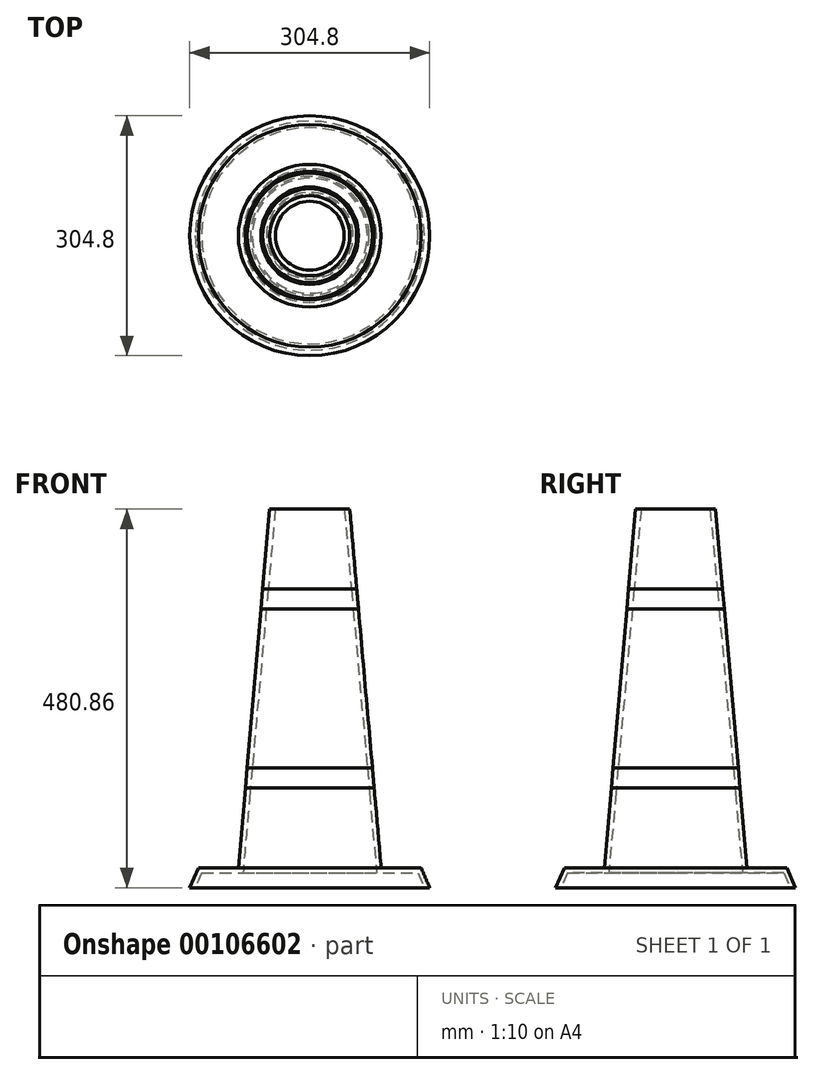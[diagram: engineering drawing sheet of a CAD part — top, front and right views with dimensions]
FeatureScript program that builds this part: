
annotation { "Feature Type Name" : "Feature", "Feature Type Description" : "" }
export const myFeature = defineFeature(function(context is Context, id is Id, definition is map)
    precondition{}
    {
        {
            var Q0;
            Q0=qCreatedBy(makeId("Front.planeOp"),FACE);
            var sketch = newSketch(context, id + "F0", { "sketchPlane" : qUnion([Q0])});
            skLineSegment(sketch, "E0", {"start": v(0, 498.76) * mm, "end": v(0, -56.63) * mm, "construction": true});
            skLineSegment(sketch, "E1", {"start": v(-152.4, 0) * mm, "end": v(-141.45, 25.4) * mm});
            skLineSegment(sketch, "E2", {"start": v(-141.45, 25.4) * mm, "end": v(-90.65, 25.4) * mm});
            skLineSegment(sketch, "E3", {"start": v(-90.65, 25.4) * mm, "end": v(-50.8, 480.86) * mm});
            skLineSegment(sketch, "E4", {"start": v(-50.8, 480.86) * mm, "end": v(0, 480.86) * mm});
            skLineSegment(sketch, "E5", {"start": v(0, 480.86) * mm, "end": v(0, 0) * mm});
            skLineSegment(sketch, "E6", {"start": v(0, 0) * mm, "end": v(-152.4, 0) * mm});
            skLineSegment(sketch, "E7", {"start": v(-59.69, 379.26) * mm, "end": v(0, 379.26) * mm});
            skLineSegment(sketch, "E8", {"start": v(-61.91, 353.86) * mm, "end": v(0, 353.86) * mm});
            skLineSegment(sketch, "E9", {"start": v(-79.54, 152.4) * mm, "end": v(0, 152.4) * mm});
            skLineSegment(sketch, "E10", {"start": v(-81.76, 127) * mm, "end": v(0, 127) * mm});
            skLineSegment(sketch, "E11", {"start": v(0, 127) * mm, "end": v(0, 152.4) * mm});
            skLineSegment(sketch, "E12", {"start": v(-81.76, 127) * mm, "end": v(-79.54, 152.4) * mm});
            skSolve(sketch);
        }
        {
            var Q0;
            Q0=makeQuery(id+"F0.imprint","IMPRINT",FACE,{"disambiguationData":[TD([[makeQuery(id+"F0.imprint","IMPRINT",EDGE,{"derivedFrom":sQuery(id+"F0.wireOp",EDGE,"E1")}),-1.0]])]});
            var Q1;
            Q1=sQuery(id+"F0.wireOp",EDGE,"E5");
            revolve(context, id + "F1", {"entities" : qUnion([Q0]), "axis" : qUnion([Q1]), "revolveType" : RevolveType.FULL});
        }
        {
            var Q0;
            Q0=makeQuery(id+"F0.imprint","IMPRINT",FACE,{"disambiguationData":[TD([[makeQuery(id+"F0.imprint","IMPRINT",EDGE,{"derivedFrom":sQuery(id+"F0.wireOp",EDGE,"E9")}),-1.0]])]});
            var Q1;
            Q1=sQuery(id+"F0.wireOp",EDGE,"E5");
            revolve(context, id + "F2", {"entities" : qUnion([Q0]), "axis" : qUnion([Q1]), "revolveType" : RevolveType.FULL});
        }
        {
            var Q0;
            {var subQ0=sQuery(id+"F0.wireOp",EDGE,"E8");Q0=makeQuery(id+"F0.imprint","IMPRINT",FACE,{"disambiguationData":[TD([[makeQuery(id+"F0.imprint","IMPRINT",EDGE,{"derivedFrom":subQ0}),-1.0]])]});}
            var Q1;
            Q1=sQuery(id+"F0.wireOp",EDGE,"E5");
            revolve(context, id + "F3", {"entities" : qUnion([Q0]), "axis" : qUnion([Q1]), "revolveType" : RevolveType.FULL});
        }
        {
            var Q0;
            {var subQ0=sQuery(id+"F0.wireOp",EDGE,"E7");Q0=makeQuery(id+"F0.imprint","IMPRINT",FACE,{"disambiguationData":[TD([[makeQuery(id+"F0.imprint","IMPRINT",EDGE,{"derivedFrom":subQ0}),-1.0]])]});}
            var Q1;
            Q1=sQuery(id+"F0.wireOp",EDGE,"E5");
            revolve(context, id + "F4", {"entities" : qUnion([Q0]), "axis" : qUnion([Q1]), "revolveType" : RevolveType.FULL});
        }
        {
            var Q0;
            {var subQ0=sQuery(id+"F0.wireOp",EDGE,"E4");Q0=makeQuery(id+"F0.imprint","IMPRINT",FACE,{"disambiguationData":[TD([[makeQuery(id+"F0.imprint","IMPRINT",EDGE,{"derivedFrom":subQ0}),-1.0]])]});}
            var Q1;
            Q1=sQuery(id+"F0.wireOp",EDGE,"E5");
            revolve(context, id + "F5", {"entities" : qUnion([Q0]), "axis" : qUnion([Q1]), "revolveType" : RevolveType.FULL});
        }
        {
            var Q0;
            Q0=makeQuery(id+"F1.opRevolve","SWEPT_FACE",FACE,{"disambiguationData":[OSD([sQuery(id+"F0.wireOp",EDGE,"E6")])]});
            shell(context, id + "F6", {"entities" : qUnion([Q0]), "thickness" : 6.35 * mm});
        }
        {
            var Q0;
            Q0=makeQuery(id+"F6.opShell","OFFSET_FACE",FACE,{"disambiguationData":[OSD([sQuery(id+"F0.wireOp",EDGE,"E10")])]});
            var sketch = newSketch(context, id + "F7", { "sketchPlane" : qUnion([Q0])});
            skCircle(sketch, "E13", {"center": v(0, 0) * mm, "radius": 75.93 * mm});
            skSolve(sketch);
        }
        {
            var Q0;
            Q0=makeQuery(id+"F7.imprint","IMPRINT",FACE,{"disambiguationData":[TD([[makeQuery(id+"F7.imprint","IMPRINT",EDGE,{"derivedFrom":sQuery(id+"F7.wireOp",EDGE,"E13")}),1.0]])]});
            extrude(context, id + "F8", {"entities" : qUnion([Q0]), "operationType" : NewBodyOperationType.REMOVE, "endBound" : BoundingType.THROUGH_ALL, "oppositeDirection" : true, "depth" : 25.4 * mm, "hasDraft" : true, "draftAngle" : 5.1 * degree, "draftPullDirection" : true});
        }
    });
